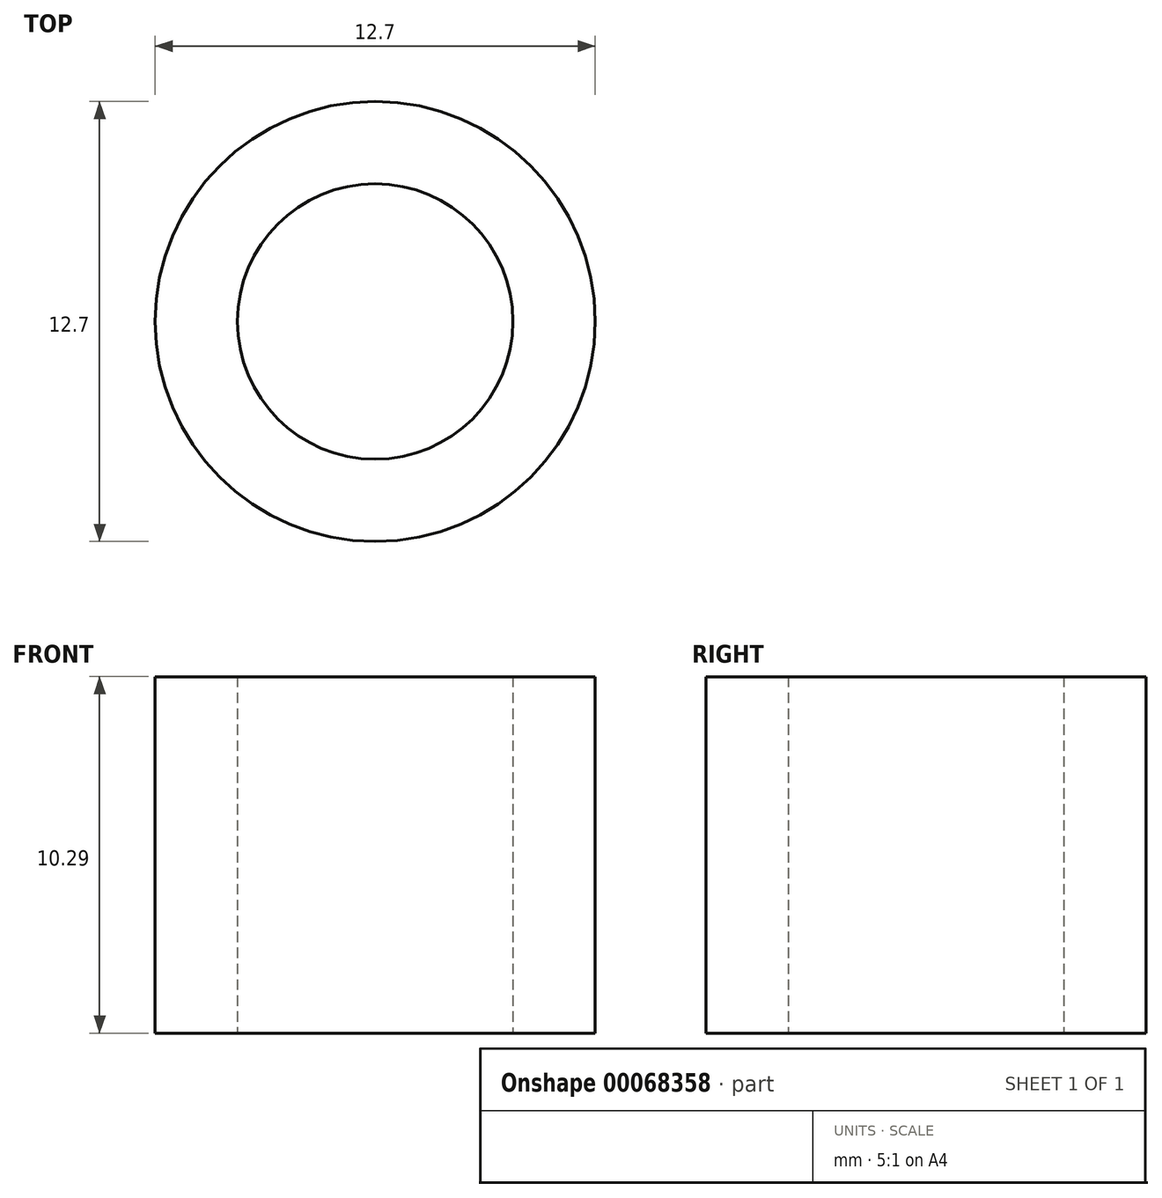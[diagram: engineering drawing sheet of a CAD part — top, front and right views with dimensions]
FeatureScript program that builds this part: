
annotation { "Feature Type Name" : "Feature", "Feature Type Description" : "" }
export const myFeature = defineFeature(function(context is Context, id is Id, definition is map)
    precondition{}
    {
        {
            var Q0;
            Q0=qCreatedBy(makeId("Top.planeOp"),FACE);
            var sketch = newSketch(context, id + "F0", { "sketchPlane" : qUnion([Q0])});
            skCircle(sketch, "E0", {"center": v(0, 0) * mm, "radius": 6.35 * mm});
            skCircle(sketch, "E1", {"center": v(0, 0) * mm, "radius": 3.98 * mm});
            skSolve(sketch);
        }
        {
            var Q0;
            Q0 = qSketchRegion(id + "F0", true);
            extrude(context, id + "F1", {"entities" : qUnion([Q0]), "depth" : 10.29 * mm});
        }
    });
